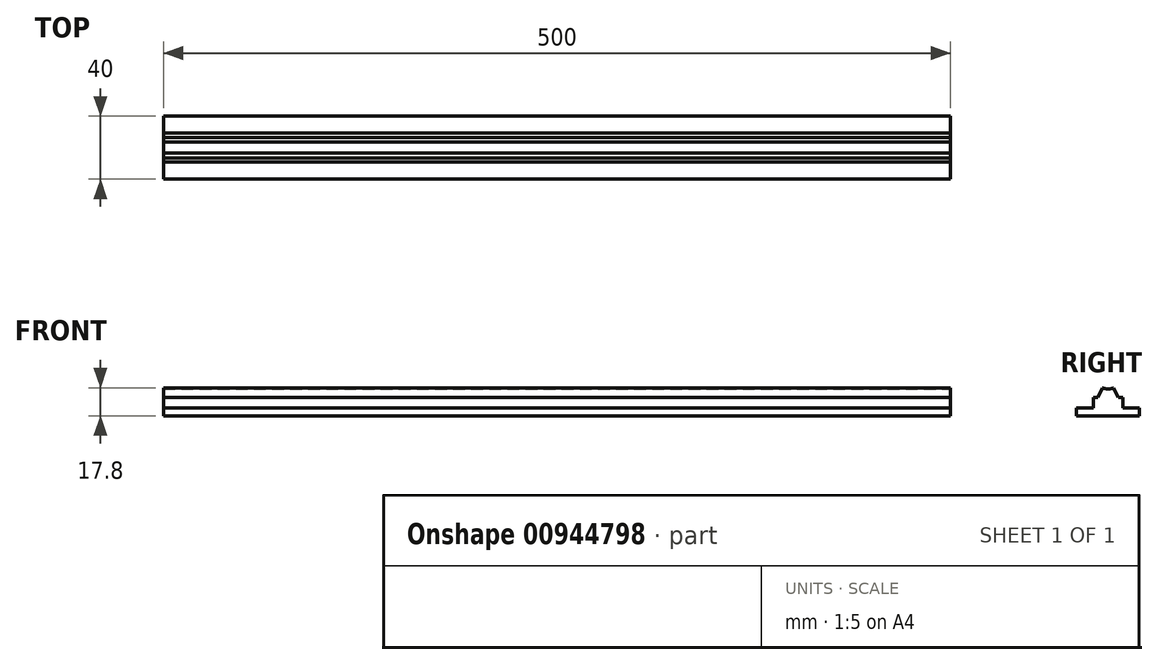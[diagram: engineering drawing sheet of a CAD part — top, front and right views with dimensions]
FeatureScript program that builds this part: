
annotation { "Feature Type Name" : "Feature", "Feature Type Description" : "" }
export const myFeature = defineFeature(function(context is Context, id is Id, definition is map)
    precondition{}
    {
        {
            var Q0;
            Q0=qCreatedBy(makeId("Top.planeOp"),FACE);
            var sketch = newSketch(context, id + "F0", { "sketchPlane" : qUnion([Q0])});
            skLineSegment(sketch, "E0.bottom", {"start": v(250, -20) * mm, "end": v(-250, -20) * mm});
            skLineSegment(sketch, "E0.top", {"start": v(250, 20) * mm, "end": v(-250, 20) * mm});
            skLineSegment(sketch, "E0.left", {"start": v(250, -20) * mm, "end": v(250, 20) * mm});
            skLineSegment(sketch, "E0.right", {"start": v(-250, -20) * mm, "end": v(-250, 20) * mm});
            skSolve(sketch);
        }
        {
            var Q0;
            Q0 = qSketchRegion(id + "F0", true);
            extrude(context, id + "F1", {"entities" : qUnion([Q0]), "depth" : 5 * mm, "offsetDistance" : 25 * mm});
        }
        {
            var Q0;
            Q0=makeQuery(id+"F1.opExtrude","SWEPT_FACE",FACE,{"disambiguationData":[OSD([sQuery(id+"F0.wireOp",EDGE,"E0.left")])]});
            var sketch = newSketch(context, id + "F2", { "sketchPlane" : qUnion([Q0])});
            skLineSegment(sketch, "E1", {"start": v(0, 0) * mm, "end": v(0, 17.8) * mm, "construction": true});
            skLineSegment(sketch, "E2", {"start": v(-9.25, 0) * mm, "end": v(9.25, 0) * mm});
            skLineSegment(sketch, "E3", {"start": v(-4, 17.8) * mm, "end": v(-3.49, 17.8) * mm});
            skLineSegment(sketch, "E4", {"start": v(0, 0) * mm, "end": v(0, 25) * mm, "construction": true});
            skCircle(sketch, "E5", {"center": v(0, 25) * mm, "radius": 8 * mm, "construction": true});
            skLineSegment(sketch, "E6", {"start": v(-3.49, 17.8) * mm, "end": v(-6.3, 11.98) * mm});
            skLineSegment(sketch, "E7", {"start": v(-2.22, 0) * mm, "end": v(-2.22, 11.7) * mm, "construction": true});
            skLineSegment(sketch, "E8", {"start": v(-9.25, 0) * mm, "end": v(-9.25, 11.7) * mm});
            skLineSegment(sketch, "E9", {"start": v(-9.25, 11.7) * mm, "end": v(9.25, 11.7) * mm});
            skLineSegment(sketch, "E10", {"start": v(9.25, 0) * mm, "end": v(9.25, 11.7) * mm});
            skLineSegment(sketch, "E11", {"start": v(-6.3, 11.98) * mm, "end": v(-6.44, 11.7) * mm});
            skLineSegment(sketch, "E12", {"start": v(3.49, 17.8) * mm, "end": v(5.35, 13.96) * mm});
            skLineSegment(sketch, "E13", {"start": v(5.35, 13.96) * mm, "end": v(6.44, 11.7) * mm});
            skArc(sketch, "E14", {"start": v(-3.49, 17.8) * mm, "mid": v(0, 17) * mm, "end": v(3.49, 17.8) * mm});
            skLineSegment(sketch, "E15.trimOffspring", {"start": v(3.49, 17.8) * mm, "end": v(4, 17.8) * mm});
            skSolve(sketch);
        }
        {
            var Q0;
            Q0 = qSketchRegion(id + "F2", true);
            var Q1;
            Q1=makeQuery(id+"F1.opExtrude","SWEPT_FACE",FACE,{"disambiguationData":[OSD([sQuery(id+"F0.wireOp",EDGE,"E0.right")])]});
            extrude(context, id + "F3", {"entities" : qUnion([Q0]), "operationType" : NewBodyOperationType.ADD, "endBound" : BoundingType.UP_TO_SURFACE, "oppositeDirection" : true, "depth" : 25 * mm, "endBoundEntityFace" : qUnion([Q1]), "offsetDistance" : 25 * mm});
        }
        {
            var Q0;
            Q0=makeQuery(id+"F3.boolean.opBoolean","MERGE",FACE,{"derivedFrom":[makeQuery(id+"F1.opExtrude","SWEPT_FACE",FACE,{"disambiguationData":[OSD([sQuery(id+"F0.wireOp",EDGE,"E0.right")])]}),makeQuery(id+"F3.opExtrude","CAP_FACE",FACE,{"disambiguationData":[OSD([sQuery(id+"F2.wireOp",EDGE,"E2"),sQuery(id+"F2.wireOp",EDGE,"E6"),sQuery(id+"F2.wireOp",EDGE,"E8"),sQuery(id+"F2.wireOp",EDGE,"E9"),sQuery(id+"F2.wireOp",EDGE,"E10"),sQuery(id+"F2.wireOp",EDGE,"E11"),sQuery(id+"F2.wireOp",EDGE,"E12"),sQuery(id+"F2.wireOp",EDGE,"E13"),sQuery(id+"F2.wireOp",EDGE,"E14")])],"isStart":false})]});
            var sketch = newSketch(context, id + "F4", { "sketchPlane" : qUnion([Q0])});
            skCircle(sketch, "E16", {"center": v(0, 25) * mm, "radius": 8 * mm});
            skSolve(sketch);
        }
        {
            var Q0;
            {var subQ0=sQuery(id+"F4.wireOp",EDGE,"E16");Q0=makeQuery(id+"F4.imprint","IMPRINT",FACE,{"disambiguationData":[TD([[makeQuery(id+"F4.imprint","IMPRINT",EDGE,{"disambiguationData":[OD(0.0)],"derivedFrom":subQ0}),1.0]])]});}
            var Q1;
            Q1=makeQuery(id+"F3.boolean.opBoolean","MERGE",FACE,{"derivedFrom":[makeQuery(id+"F1.opExtrude","SWEPT_FACE",FACE,{"disambiguationData":[OSD([sQuery(id+"F0.wireOp",EDGE,"E0.left")])]}),makeQuery(id+"F3.opExtrude","CAP_FACE",FACE,{"disambiguationData":[OSD([sQuery(id+"F2.wireOp",EDGE,"E2"),sQuery(id+"F2.wireOp",EDGE,"E6"),sQuery(id+"F2.wireOp",EDGE,"E8"),sQuery(id+"F2.wireOp",EDGE,"E9"),sQuery(id+"F2.wireOp",EDGE,"E10"),sQuery(id+"F2.wireOp",EDGE,"E11"),sQuery(id+"F2.wireOp",EDGE,"E12"),sQuery(id+"F2.wireOp",EDGE,"E13"),sQuery(id+"F2.wireOp",EDGE,"E14")])],"isStart":true})]});
            extrude(context, id + "F5", {"entities" : qUnion([Q0]), "operationType" : NewBodyOperationType.ADD, "endBound" : BoundingType.UP_TO_SURFACE, "oppositeDirection" : true, "depth" : 25 * mm, "endBoundEntityFace" : qUnion([Q1]), "offsetDistance" : 25 * mm});
        }
    });
